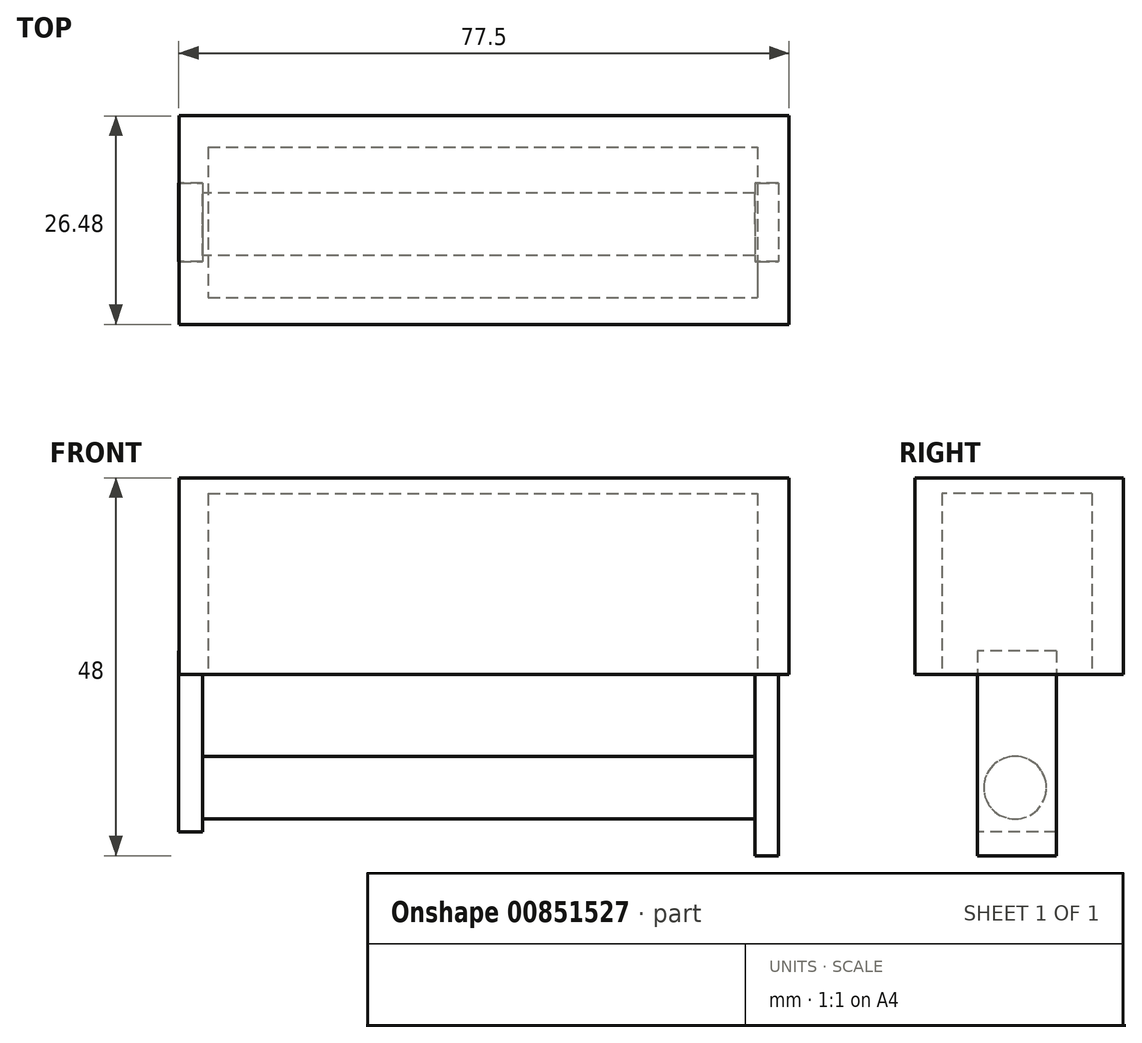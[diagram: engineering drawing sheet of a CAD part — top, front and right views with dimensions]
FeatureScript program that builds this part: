
annotation { "Feature Type Name" : "Feature", "Feature Type Description" : "" }
export const myFeature = defineFeature(function(context is Context, id is Id, definition is map)
    precondition{}
    {
        {
            var Q0;
            Q0=qCreatedBy(makeId("Top.planeOp"),FACE);
            var sketch = newSketch(context, id + "F0", { "sketchPlane" : qUnion([Q0])});
            skLineSegment(sketch, "E0.bottom", {"start": v(-22.64, 18.51) * mm, "end": v(54.83, 18.51) * mm});
            skLineSegment(sketch, "E0.top", {"start": v(-22.64, -7.97) * mm, "end": v(54.83, -7.97) * mm});
            skLineSegment(sketch, "E0.left", {"start": v(-22.64, 18.51) * mm, "end": v(-22.64, -7.97) * mm});
            skLineSegment(sketch, "E0.right", {"start": v(54.83, 18.51) * mm, "end": v(54.83, -7.97) * mm});
            skSolve(sketch);
        }
        {
            var Q0;
            Q0 = qSketchRegion(id + "F0", true);
            extrude(context, id + "F1", {"entities" : qUnion([Q0]), "depth" : 25 * mm, "offsetDistance" : 25 * mm});
        }
        {
            var Q0;
            Q0=qCreatedBy(makeId("Top.planeOp"),FACE);
            var sketch = newSketch(context, id + "F2", { "sketchPlane" : qUnion([Q0])});
            skLineSegment(sketch, "E1.bottom", {"start": v(-18.94, 14.53) * mm, "end": v(50.84, 14.53) * mm});
            skLineSegment(sketch, "E1.top", {"start": v(-18.94, -4.56) * mm, "end": v(50.84, -4.56) * mm});
            skLineSegment(sketch, "E1.left", {"start": v(-18.94, 14.53) * mm, "end": v(-18.94, -4.56) * mm});
            skLineSegment(sketch, "E1.right", {"start": v(50.84, 14.53) * mm, "end": v(50.84, -4.56) * mm});
            skSolve(sketch);
        }
        {
            var Q0;
            Q0 = qSketchRegion(id + "F2", true);
            extrude(context, id + "F3", {"entities" : qUnion([Q0]), "operationType" : NewBodyOperationType.REMOVE, "depth" : 23 * mm, "offsetDistance" : 25 * mm});
        }
        {
            var Q0;
            Q0=qCreatedBy(makeId("Front.planeOp"),FACE);
            var sketch = newSketch(context, id + "F4", { "sketchPlane" : qUnion([Q0])});
            skLineSegment(sketch, "E2.bottom", {"start": v(-19.67, 3.02) * mm, "end": v(-22.67, 3.02) * mm});
            skLineSegment(sketch, "E2.top", {"start": v(-19.67, -19.98) * mm, "end": v(-22.67, -19.98) * mm});
            skLineSegment(sketch, "E2.left", {"start": v(-19.67, 3.02) * mm, "end": v(-19.67, -19.98) * mm});
            skLineSegment(sketch, "E2.right", {"start": v(-22.67, 3.02) * mm, "end": v(-22.67, -19.98) * mm});
            skLineSegment(sketch, "E3", {"start": v(53.5, 0) * mm, "end": v(53.5, -23) * mm});
            skLineSegment(sketch, "E4", {"start": v(53.5, -23) * mm, "end": v(50.5, -23) * mm});
            skLineSegment(sketch, "E5", {"start": v(50.5, -23) * mm, "end": v(50.5, 0) * mm});
            skLineSegment(sketch, "E6", {"start": v(50.5, 0) * mm, "end": v(53.5, 0) * mm});
            skSolve(sketch);
        }
        {
            var Q0;
            Q0 = qSketchRegion(id + "F4", true);
            extrude(context, id + "F5", {"entities" : qUnion([Q0]), "operationType" : NewBodyOperationType.ADD, "oppositeDirection" : true, "depth" : 10 * mm, "offsetDistance" : 25 * mm});
        }
        {
            var Q0;
            Q0=makeQuery(id+"F5.opExtrude","SWEPT_FACE",FACE,{"disambiguationData":[OSD([sQuery(id+"F4.wireOp",EDGE,"E2.left")])]});
            var sketch = newSketch(context, id + "F6", { "sketchPlane" : qUnion([Q0])});
            skCircle(sketch, "E7", {"center": v(4.75, -14.37) * mm, "radius": 3.97 * mm});
            skSolve(sketch);
        }
        {
            var Q0;
            Q0 = qSketchRegion(id + "F6", true);
            extrude(context, id + "F7", {"entities" : qUnion([Q0]), "operationType" : NewBodyOperationType.ADD, "depth" : 72 * mm, "offsetDistance" : 25 * mm});
        }
    });
